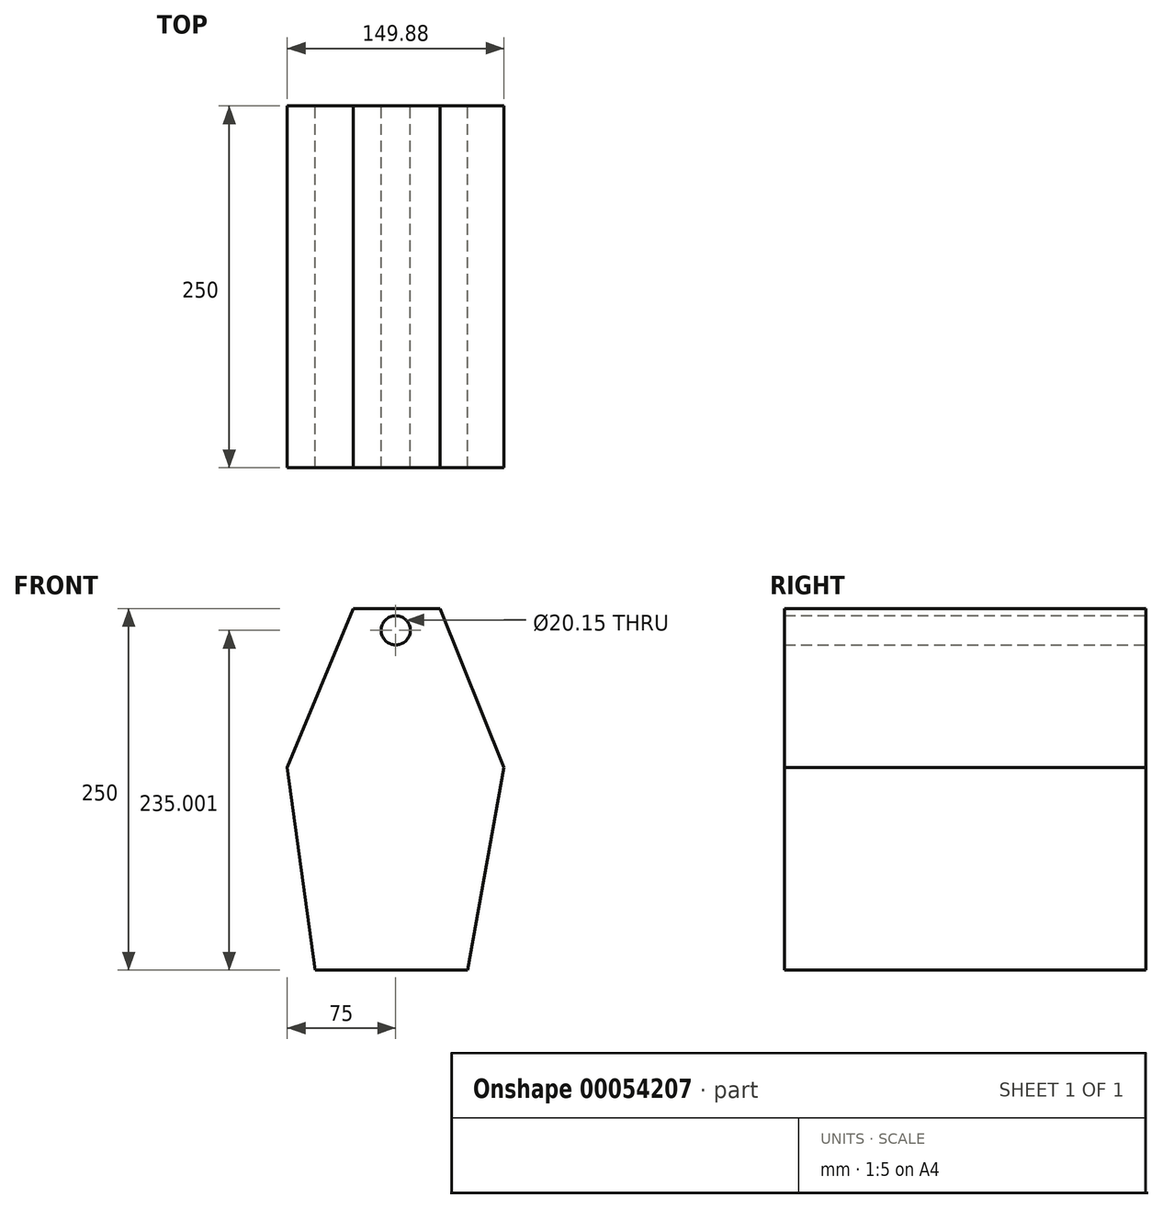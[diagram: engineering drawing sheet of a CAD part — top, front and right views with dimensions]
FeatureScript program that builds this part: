
annotation { "Feature Type Name" : "Feature", "Feature Type Description" : "" }
export const myFeature = defineFeature(function(context is Context, id is Id, definition is map)
    precondition{}
    {
        {
            var Q0;
            Q0=qCreatedBy(makeId("Front.planeOp"),FACE);
            var sketch = newSketch(context, id + "F0", { "sketchPlane" : qUnion([Q0])});
            skLineSegment(sketch, "E0", {"start": v(-29.35, 130.3) * mm, "end": v(30.65, 130.3) * mm});
            skLineSegment(sketch, "E1.0", {"start": v(-55.8, -119.7) * mm, "end": v(49.86, -119.7) * mm});
            skPoint(sketch, "E2", {"position": v(20, 19.88) * mm});
            skLineSegment(sketch, "E3", {"start": v(-29.35, 130.3) * mm, "end": v(-75, 20.3) * mm});
            skLineSegment(sketch, "E4", {"start": v(-75, 20.3) * mm, "end": v(-55.8, -119.7) * mm});
            skLineSegment(sketch, "E5", {"start": v(30.65, 130.3) * mm, "end": v(74.88, 20.3) * mm});
            skLineSegment(sketch, "E6", {"start": v(74.88, 20.3) * mm, "end": v(49.86, -119.7) * mm});
            skCircle(sketch, "E7", {"center": v(0, 115.3) * mm, "radius": 15 * mm});
            skPoint(sketch, "E8.start.orphan", {"position": v(0, 130.3) * mm});
            skCircle(sketch, "E9", {"center": v(0, 115.3) * mm, "radius": 10.08 * mm});
            skSolve(sketch);
        }
        {
            var Q0;
            Q0 = qSketchRegion(id + "F0", true);
            extrude(context, id + "F1", {"entities" : qUnion([Q0]), "depth" : 250 * mm});
        }
    });
